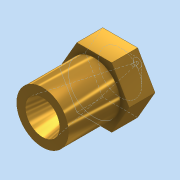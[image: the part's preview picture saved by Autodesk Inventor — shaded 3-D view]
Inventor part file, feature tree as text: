
AUTODESK INVENTOR PART (.ipt)
format: ipt  version: 2016 (Build 200138000, 138)  size: 137,728 bytes
history: native  units: mm
features: sketch x4, extrude x3, chamfer x1, hole x1
ambient origin geometry x8: Origin, YZ Plane, XZ Plane, XY Plane, X Axis, Y Axis, Z Axis, Center Point
bodies: Solid1 (feature_tree)
feature tree (9):
  extrude  "Extrusion1"  Depth=6.0mm TaperAngle=0.0deg
  extrude  "Extrusion2"  Depth=3.0mm TaperAngle=0.0deg
  extrude  "Extrusion3"  Depth=2.0mm TaperAngle=0.0deg
  chamfer  "Chamfer1"  Distance=2.0mm Angle=45.0deg
  hole  "Hole1"  [1 undecoded]
  sketch  "Sketch1"  dims[d0=6.0mm d1=6.0mm d2=0.0mm]
  sketch  "Sketch2"  dims[d3=7.0mm d4=3.0mm d5=0.0mm]
  sketch  "Sketch3"  dims[d6=5.0mm d7=2.0mm d8=0.0mm d9=2.0mm d10=2.0mm d11=45.0deg]
  sketch  "Sketch4"  dims[d12=0.3mm d13=6.0mm d14=4.0mm d15=2.0mm d16=3.490659mm d17=8.0mm d18=20.594885mm]
note: 1 required parameter value undecoded (feature->parameter linkage not recoverable at this tier; creation-order binding heuristic only, values carry confidence <= 0.55)
